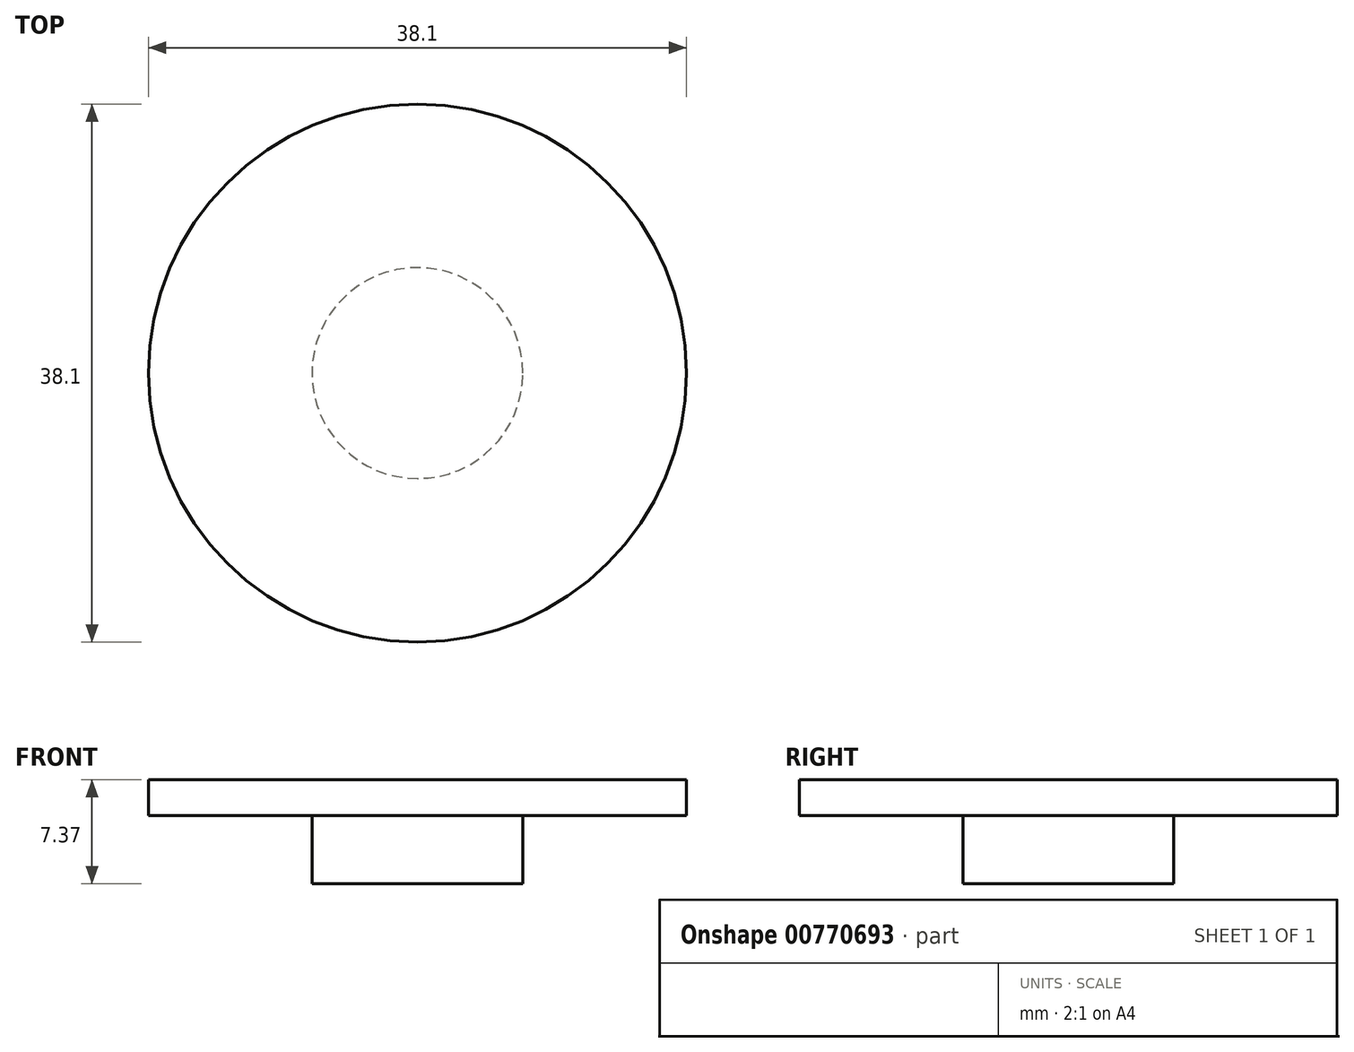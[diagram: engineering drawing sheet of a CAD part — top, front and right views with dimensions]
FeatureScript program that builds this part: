
annotation { "Feature Type Name" : "Feature", "Feature Type Description" : "" }
export const myFeature = defineFeature(function(context is Context, id is Id, definition is map)
    precondition{}
    {
        {
            var Q0;
            Q0=qCreatedBy(makeId("Top.planeOp"),FACE);
            var sketch = newSketch(context, id + "F0", { "sketchPlane" : qUnion([Q0])});
            skCircle(sketch, "E0", {"center": v(0, 0) * mm, "radius": 19.05 * mm});
            skCircle(sketch, "E1", {"center": v(0, 0) * mm, "radius": 2.25 * mm});
            skSolve(sketch);
        }
        {
            var Q0;
            Q0=makeQuery(id+"F0.imprint","IMPRINT",FACE,{"disambiguationData":[TD([[makeQuery(id+"F0.imprint","IMPRINT",EDGE,{"derivedFrom":sQuery(id+"F0.wireOp",EDGE,"E1")}),1.0]])]});
            extrude(context, id + "F1", {"entities" : qUnion([Q0]), "depth" : 2.54 * mm, "offsetDistance" : 25.4 * mm});
        }
        {
            var Q0;
            Q0 = qSketchRegion(id + "F0", true);
            extrude(context, id + "F2", {"entities" : qUnion([Q0]), "operationType" : NewBodyOperationType.ADD, "depth" : 2.54 * mm, "offsetDistance" : 25.4 * mm});
        }
        {
            var Q0;
            {var subQ0=sQuery(id+"F0.wireOp",EDGE,"E1");Q0=makeQuery(id+"F2.boolean.opBoolean","MERGE",FACE,{"derivedFrom":[makeQuery(id+"F1.opExtrude","CAP_FACE",FACE,{"disambiguationData":[OSD([subQ0])],"isStart":true}),makeQuery(id+"F2.opExtrude","CAP_FACE",FACE,{"disambiguationData":[OSD([sQuery(id+"F0.wireOp",EDGE,"E0"),subQ0])],"isStart":true})]});}
            var sketch = newSketch(context, id + "F3", { "sketchPlane" : qUnion([Q0])});
            skCircle(sketch, "E2", {"center": v(0, 0) * mm, "radius": 7.47 * mm});
            skSolve(sketch);
        }
        {
            var Q0;
            Q0=makeQuery(id+"F3.imprint","IMPRINT",FACE,{"disambiguationData":[TD([[makeQuery(id+"F3.imprint","IMPRINT",EDGE,{"derivedFrom":sQuery(id+"F3.wireOp",EDGE,"E2")}),1.0]])]});
            extrude(context, id + "F4", {"entities" : qUnion([Q0]), "operationType" : NewBodyOperationType.ADD, "depth" : 4.83 * mm, "offsetDistance" : 25.4 * mm});
        }
    });
